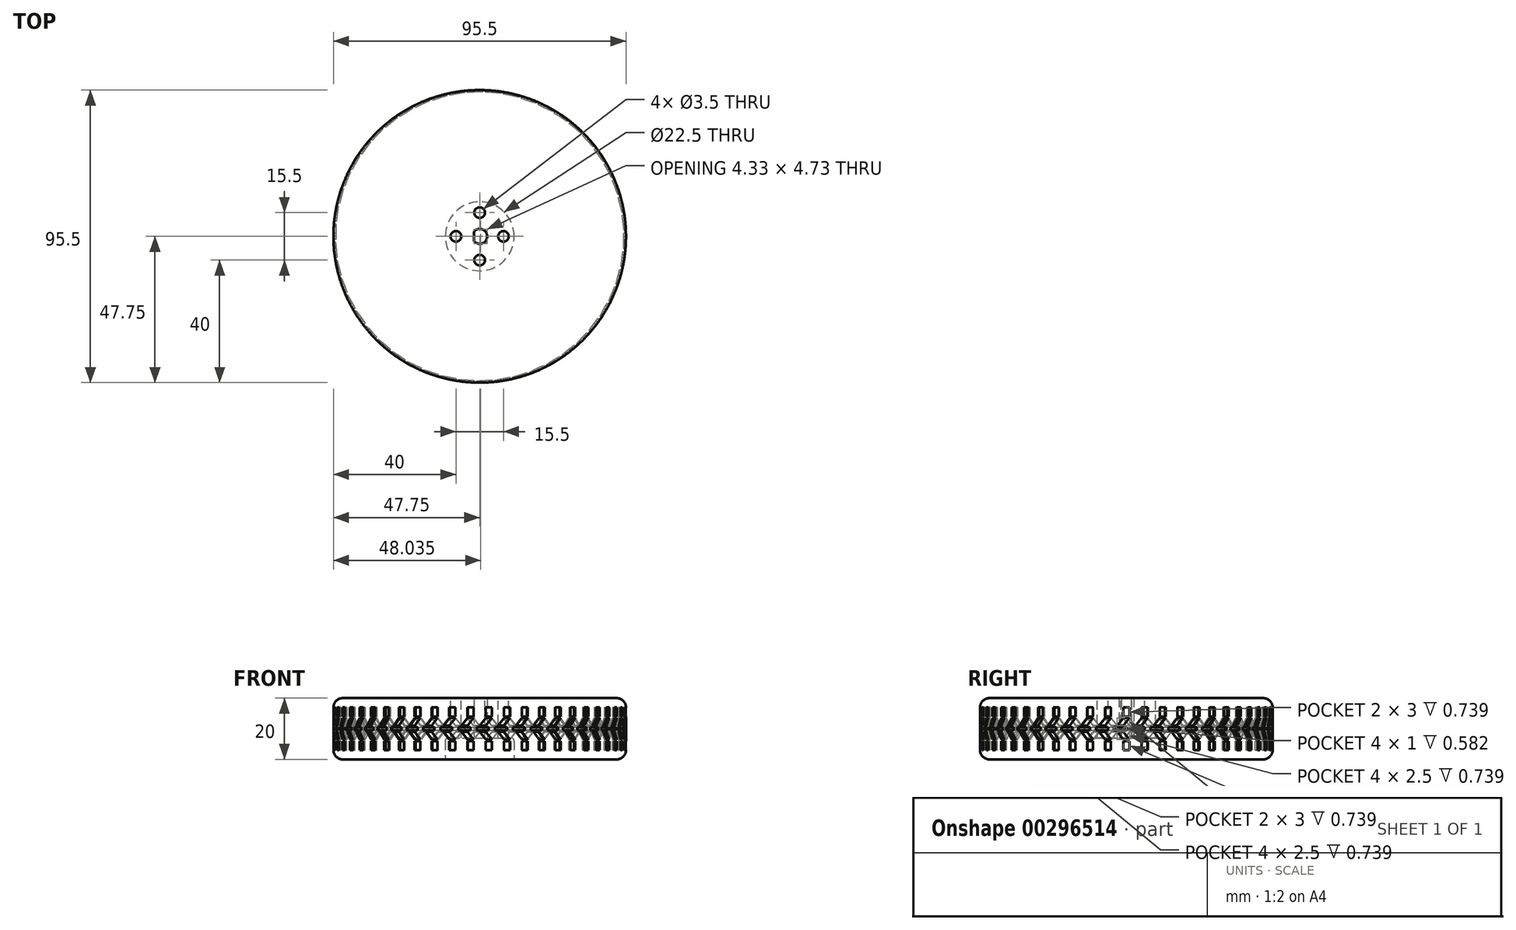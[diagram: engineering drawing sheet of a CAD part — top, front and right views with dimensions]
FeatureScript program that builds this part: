
annotation { "Feature Type Name" : "Feature", "Feature Type Description" : "" }
export const myFeature = defineFeature(function(context is Context, id is Id, definition is map)
    precondition{}
    {
        {
            assignVariable(context, id + "F0", {"name" : "TreadCount", "anyValue" : 50});
        }
        {
            var Q0;
            Q0=qCreatedBy(makeId("Top.planeOp"),FACE);
            var sketch = newSketch(context, id + "F1", { "sketchPlane" : qUnion([Q0])});
            skCircle(sketch, "E0", {"center": v(0, 0) * mm, "radius": 47.75 * mm});
            skCircle(sketch, "E1", {"center": v(0, 0) * mm, "radius": 44 * mm});
            skArc(sketch, "E2", {"start": v(-1.88, -1.57) * mm, "mid": v(2.45, 0) * mm, "end": v(-1.88, 1.57) * mm});
            skLineSegment(sketch, "E3", {"start": v(-1.88, -1.57) * mm, "end": v(-1.88, 1.57) * mm});
            skCircle(sketch, "E4", {"center": v(0, 0) * mm, "radius": 42.5 * mm});
            skCircle(sketch, "E5", {"center": v(0, 0) * mm, "radius": 36 * mm});
            skSolve(sketch);
        }
        {
            var Q0;
            Q0=makeQuery(id+"F1.imprint","IMPRINT",FACE,{"disambiguationData":[TD([[makeQuery(id+"F1.imprint","IMPRINT",EDGE,{"derivedFrom":sQuery(id+"F1.wireOp",EDGE,"E2")}),-1.0]])]});
            var Q1;
            Q1=makeQuery(id+"F1.imprint","IMPRINT",FACE,{"disambiguationData":[TD([[makeQuery(id+"F1.imprint","IMPRINT",EDGE,{"derivedFrom":sQuery(id+"F1.wireOp",EDGE,"8wvdLqEF-Mvgu-ieMB-92kP-JiN9EquYggHF")}),1.0]])]});
            extrude(context, id + "F2", {"entities" : qUnion([Q0, Q1]), "depth" : 12.5 * mm, "hasSecondDirection" : true, "secondDirectionOppositeDirection" : false, "secondDirectionDepth" : 7.5 * mm});
        }
        {
            var Q0;
            Q0=makeQuery(id+"F1.imprint","IMPRINT",FACE,{"disambiguationData":[TD([[makeQuery(id+"F1.imprint","IMPRINT",EDGE,{"derivedFrom":sQuery(id+"F1.wireOp",EDGE,"E4")}),1.0]])]});
            var Q1;
            Q1=makeQuery(id+"F1.imprint","IMPRINT",FACE,{"disambiguationData":[TD([[makeQuery(id+"F1.imprint","IMPRINT",EDGE,{"derivedFrom":sQuery(id+"F1.wireOp",EDGE,"E1")}),1.0]])]});
            var Q2;
            Q2=makeQuery(id+"F1.imprint","IMPRINT",FACE,{"disambiguationData":[TD([[makeQuery(id+"F1.imprint","IMPRINT",EDGE,{"derivedFrom":sQuery(id+"F1.wireOp",EDGE,"E2")}),-1.0]])]});
            extrude(context, id + "F3", {"entities" : qUnion([Q0, Q1, Q2]), "operationType" : NewBodyOperationType.ADD, "depth" : 20 * mm});
        }
        {
            var Q0;
            Q0=makeQuery(id+"F1.imprint","IMPRINT",FACE,{"disambiguationData":[TD([[makeQuery(id+"F1.imprint","IMPRINT",EDGE,{"derivedFrom":sQuery(id+"F1.wireOp",EDGE,"E0")}),1.0]])]});
            extrude(context, id + "F4", {"entities" : qUnion([Q0]), "depth" : 20 * mm});
        }
        {
            var Q0;
            Q0=makeQuery(id+"F1.imprint","IMPRINT",FACE,{"disambiguationData":[TD([[makeQuery(id+"F1.imprint","IMPRINT",EDGE,{"derivedFrom":sQuery(id+"F1.wireOp",EDGE,"E1")}),1.0]])]});
            extrude(context, id + "F5", {"entities" : qUnion([Q0]), "operationType" : NewBodyOperationType.REMOVE, "depth" : 1 * mm});
        }
        {
            var Q0;
            Q0=makeQuery(id+"F1.imprint","IMPRINT",FACE,{"disambiguationData":[TD([[makeQuery(id+"F1.imprint","IMPRINT",EDGE,{"derivedFrom":sQuery(id+"F1.wireOp",EDGE,"E1")}),1.0]])]});
            extrude(context, id + "F6", {"entities" : qUnion([Q0]), "operationType" : NewBodyOperationType.ADD, "depth" : 1 * mm});
        }
        {
            var Q0;
            Q0=makeQuery(id+"F1.imprint","IMPRINT",FACE,{"disambiguationData":[TD([[makeQuery(id+"F1.imprint","IMPRINT",EDGE,{"derivedFrom":sQuery(id+"F1.wireOp",EDGE,"E1")}),1.0]])]});
            extrude(context, id + "F7", {"entities" : qUnion([Q0]), "operationType" : NewBodyOperationType.REMOVE, "depth" : 20 * mm, "hasSecondDirection" : true, "secondDirectionOppositeDirection" : false, "secondDirectionDepth" : 19 * mm});
        }
        {
            var Q0;
            Q0=makeQuery(id+"F1.imprint","IMPRINT",FACE,{"disambiguationData":[TD([[makeQuery(id+"F1.imprint","IMPRINT",EDGE,{"derivedFrom":sQuery(id+"F1.wireOp",EDGE,"E1")}),1.0]])]});
            extrude(context, id + "F8", {"entities" : qUnion([Q0]), "operationType" : NewBodyOperationType.ADD, "depth" : 20 * mm, "hasSecondDirection" : true, "secondDirectionOppositeDirection" : false, "secondDirectionDepth" : 19 * mm});
        }
        {
            var Q0;
            Q0=qCreatedBy(makeId("Right.planeOp"),FACE);
            cPlane(context, id + "F9", {"entities" : qUnion([Q0]), "cplaneType" : CPlaneType.OFFSET, "offset" : 48 * mm, "width" : 150 * mm, "height" : 150 * mm});
        }
        {
            var Q0;
            Q0=qCreatedBy(id+"F9.planeOp",FACE);
            var sketch = newSketch(context, id + "F10", { "sketchPlane" : qUnion([Q0])});
            skPoint(sketch, "E6", {"position": v(0, 10) * mm});
            skLineSegment(sketch, "E7.bottom", {"start": v(-1, 17) * mm, "end": v(1, 17) * mm});
            skLineSegment(sketch, "E7.top", {"start": v(-1, 14) * mm, "end": v(1, 14) * mm});
            skLineSegment(sketch, "E7.left", {"start": v(-1, 17) * mm, "end": v(-1, 14) * mm});
            skLineSegment(sketch, "E7.right", {"start": v(1, 17) * mm, "end": v(1, 14) * mm});
            skLineSegment(sketch, "E8", {"start": v(0, 10) * mm, "end": v(-8.56, 10) * mm});
            skLineSegment(sketch, "E9.MirrorCS", {"start": v(-1, 6) * mm, "end": v(1, 6) * mm});
            skLineSegment(sketch, "E10.MirrorCS", {"start": v(-1, 3) * mm, "end": v(-1, 6) * mm});
            skLineSegment(sketch, "E11.MirrorCS", {"start": v(1, 3) * mm, "end": v(1, 6) * mm});
            skLineSegment(sketch, "E12.MirrorCS", {"start": v(-1, 3) * mm, "end": v(1, 3) * mm});
            skLineSegment(sketch, "E13.bottom", {"start": v(-1, 13.5) * mm, "end": v(1, 13.5) * mm});
            skPoint(sketch, "E14", {"position": v(-3, 11) * mm});
            skLineSegment(sketch, "E15", {"start": v(-3, 11) * mm, "end": v(-1, 13.5) * mm});
            skLineSegment(sketch, "E16.MirrorCS", {"start": v(-3, 9) * mm, "end": v(-1, 6.5) * mm});
            skLineSegment(sketch, "E17.MirrorCS", {"start": v(-1, 6.5) * mm, "end": v(1, 6.5) * mm});
            skPoint(sketch, "E18", {"position": v(-1, 11) * mm});
            skLineSegment(sketch, "E19", {"start": v(-3, 11) * mm, "end": v(-1, 11) * mm});
            skLineSegment(sketch, "E20", {"start": v(-1, 11) * mm, "end": v(1, 13.5) * mm});
            skLineSegment(sketch, "E21.MirrorCS", {"start": v(-3, 9) * mm, "end": v(-1, 9) * mm});
            skLineSegment(sketch, "E22.MirrorCS", {"start": v(-1, 9) * mm, "end": v(1, 6.5) * mm});
            skLineSegment(sketch, "E23.bottom", {"start": v(-4, 10.5) * mm, "end": v(0, 10.5) * mm});
            skLineSegment(sketch, "E23.top", {"start": v(-4, 9.5) * mm, "end": v(0, 9.5) * mm});
            skLineSegment(sketch, "E23.left", {"start": v(-4, 10.5) * mm, "end": v(-4, 9.5) * mm});
            skLineSegment(sketch, "E23.right", {"start": v(0, 10.5) * mm, "end": v(0, 9.5) * mm});
            skPoint(sketch, "E23.middle", {"position": v(-2, 10) * mm});
            skSolve(sketch);
        }
        {
            var Q0;
            Q0=makeQuery(id+"F10.imprint","IMPRINT",FACE,{"disambiguationData":[TD([[makeQuery(id+"F10.imprint","IMPRINT",EDGE,{"derivedFrom":sQuery(id+"F10.wireOp",EDGE,"E7.bottom")}),-1.0]])]});
            var Q1;
            Q1=makeQuery(id+"F10.imprint","IMPRINT",FACE,{"disambiguationData":[TD([[makeQuery(id+"F10.imprint","IMPRINT",EDGE,{"derivedFrom":sQuery(id+"F10.wireOp",EDGE,"E13.bottom")}),-1.0]])]});
            var Q2;
            Q2=makeQuery(id+"F10.imprint","IMPRINT",FACE,{"disambiguationData":[TD([[makeQuery(id+"F10.imprint","IMPRINT",EDGE,{"derivedFrom":sQuery(id+"F10.wireOp",EDGE,"c6fea6ce-3147-4b6b-9fa2-a9a93d3b0bdf0.MirrorCS")}),-1.0]])]});
            var Q3;
            Q3=makeQuery(id+"F10.imprint","IMPRINT",FACE,{"disambiguationData":[TD([[makeQuery(id+"F10.imprint","IMPRINT",EDGE,{"derivedFrom":sQuery(id+"F10.wireOp",EDGE,"E9.MirrorCS")}),-1.0]])]});
            var Q4;
            Q4=makeQuery(id+"F10.imprint","IMPRINT",FACE,{"disambiguationData":[TD([[makeQuery(id+"F10.imprint","IMPRINT",EDGE,{"derivedFrom":sQuery(id+"F10.wireOp",EDGE,"E16.MirrorCS")}),1.0]])]});
            var Q5;
            {var subQ5=sQuery(id+"F10.wireOp",EDGE,"E23.top");Q5=makeQuery(id+"F10.imprint","IMPRINT",FACE,{"disambiguationData":[TD([[makeQuery(id+"F10.imprint","IMPRINT",EDGE,{"derivedFrom":subQ5}),1.0]])]});}
            var Q6;
            {var subQ5=sQuery(id+"F10.wireOp",EDGE,"E23.bottom");Q6=makeQuery(id+"F10.imprint","IMPRINT",FACE,{"disambiguationData":[TD([[makeQuery(id+"F10.imprint","IMPRINT",EDGE,{"derivedFrom":subQ5}),-1.0]])]});}
            extrude(context, id + "F11", {"entities" : qUnion([Q0, Q1, Q2, Q3, Q4, Q5, Q6]), "oppositeDirection" : true, "depth" : 1 * mm, "hasSecondDirection" : true, "secondDirectionOppositeDirection" : false, "secondDirectionDepth" : 5 * mm});
        }
        {
            var Q0;
            Q0=makeQuery(id+"F11.opExtrude","SWEPT_BODY",BODY,{"disambiguationData":[OSD([sQuery(id+"F10.wireOp",EDGE,"E23.bottom"),sQuery(id+"F10.wireOp",EDGE,"E23.top"),sQuery(id+"F10.wireOp",EDGE,"E23.left"),sQuery(id+"F10.wireOp",EDGE,"E23.right")])]});
            var Q1;
            Q1=makeQuery(id+"F11.opExtrude","SWEPT_BODY",BODY,{"disambiguationData":[OSD([sQuery(id+"F10.wireOp",EDGE,"E13.bottom"),sQuery(id+"F10.wireOp",EDGE,"E15"),sQuery(id+"F10.wireOp",EDGE,"E19"),sQuery(id+"F10.wireOp",EDGE,"E20")])]});
            var Q2;
            Q2=makeQuery(id+"F11.opExtrude","SWEPT_BODY",BODY,{"disambiguationData":[OSD([sQuery(id+"F10.wireOp",EDGE,"E7.bottom"),sQuery(id+"F10.wireOp",EDGE,"E7.top"),sQuery(id+"F10.wireOp",EDGE,"E7.left"),sQuery(id+"F10.wireOp",EDGE,"E7.right")])]});
            var Q3;
            Q3=makeQuery(id+"F11.opExtrude","SWEPT_BODY",BODY,{"disambiguationData":[OSD([sQuery(id+"F10.wireOp",EDGE,"E16.MirrorCS"),sQuery(id+"F10.wireOp",EDGE,"E17.MirrorCS"),sQuery(id+"F10.wireOp",EDGE,"E21.MirrorCS"),sQuery(id+"F10.wireOp",EDGE,"E22.MirrorCS")])]});
            var Q4;
            Q4=makeQuery(id+"F11.opExtrude","SWEPT_BODY",BODY,{"disambiguationData":[OSD([sQuery(id+"F10.wireOp",EDGE,"E9.MirrorCS"),sQuery(id+"F10.wireOp",EDGE,"E10.MirrorCS"),sQuery(id+"F10.wireOp",EDGE,"E11.MirrorCS"),sQuery(id+"F10.wireOp",EDGE,"E12.MirrorCS")])]});
            var Q5;
            Q5=makeQuery(id+"F4.opExtrude","CAP_EDGE",EDGE,{"disambiguationData":[OSD([sQuery(id+"F1.wireOp",EDGE,"E0")])],"isStart":false});
            circularPattern(context, id + "F12", {"operationType" : NewBodyOperationType.REMOVE, "entities" : qUnion([Q0, Q1, Q2, Q3, Q4]), "axis" : qUnion([Q5]), "angle" : 360 * degree, "instanceCount" : getVariable(context, 'TreadCount'), "equalSpace" : true});
        }
        {
            var Q0;
            Q0=makeQuery(id+"F4.opExtrude","CAP_EDGE",EDGE,{"disambiguationData":[OSD([sQuery(id+"F1.wireOp",EDGE,"E0")])],"isStart":false});
            var Q1;
            Q1=makeQuery(id+"F4.opExtrude","CAP_EDGE",EDGE,{"disambiguationData":[OSD([sQuery(id+"F1.wireOp",EDGE,"E0")])],"isStart":true});
            fillet(context, id + "F13", {"entities" : qUnion([Q0, Q1]), "radius" : 3 * mm, "tangentPropagation" : true, "allowEdgeOverflow" : false});
        }
        {
            var Q0;
            Q0=makeQuery(id+"F3.opExtrude","CAP_FACE",FACE,{"disambiguationData":[OSD([sQuery(id+"F1.wireOp",EDGE,"E1"),sQuery(id+"F1.wireOp",EDGE,"E2"),sQuery(id+"F1.wireOp",EDGE,"E3")])],"isStart":true});
            var sketch = newSketch(context, id + "F14", { "sketchPlane" : qUnion([Q0])});
            skCircle(sketch, "E24", {"center": v(0, 0) * mm, "radius": 11.25 * mm});
            skCircle(sketch, "E25", {"center": v(0, 0) * mm, "radius": 2.5 * mm});
            skCircle(sketch, "E26", {"center": v(0, 7.75) * mm, "radius": 1.75 * mm});
            skSolve(sketch);
        }
        {
            var Q0;
            Q0=makeQuery(id+"F14.imprint","IMPRINT",FACE,{"disambiguationData":[TD([[makeQuery(id+"F14.imprint","IMPRINT",EDGE,{"derivedFrom":sQuery(id+"F14.wireOp",EDGE,"E24")}),1.0]])]});
            var Q1;
            Q1=makeQuery(id+"F14.imprint","IMPRINT",FACE,{"disambiguationData":[TD([[makeQuery(id+"F14.imprint","IMPRINT",EDGE,{"derivedFrom":sQuery(id+"F14.wireOp",EDGE,"E26")}),1.0]])]});
            var Q2;
            Q2=makeQuery(id+"F14.imprint","IMPRINT",FACE,{"disambiguationData":[TD([[makeQuery(id+"F14.imprint","IMPRINT",EDGE,{"derivedFrom":makeQuery(id+"F3.opExtrude","CAP_EDGE",EDGE,{"disambiguationData":[OSD([sQuery(id+"F1.wireOp",EDGE,"E2")])],"isStart":true})}),-1.0]])]});
            var Q3;
            Q3=makeQuery(id+"F14.imprint","IMPRINT",FACE,{"disambiguationData":[TD([[makeQuery(id+"F14.imprint","IMPRINT",EDGE,{"derivedFrom":sQuery(id+"F14.wireOp",EDGE,"E25")}),1.0]])]});
            extrude(context, id + "F15", {"entities" : qUnion([Q0, Q1, Q2, Q3]), "operationType" : NewBodyOperationType.REMOVE, "oppositeDirection" : true, "depth" : 7 * mm});
        }
        {
            var Q0;
            Q0=makeQuery(id+"F14.imprint","IMPRINT",FACE,{"disambiguationData":[TD([[makeQuery(id+"F14.imprint","IMPRINT",EDGE,{"derivedFrom":sQuery(id+"F14.wireOp",EDGE,"E26")}),1.0]])]});
            extrude(context, id + "F16", {"entities" : qUnion([Q0]), "depth" : 25 * mm, "hasSecondDirection" : true, "secondDirectionOppositeDirection" : true, "secondDirectionDepth" : 25 * mm});
        }
        {
            var Q0;
            Q0=makeQuery(id+"F16.opExtrude","SWEPT_BODY",BODY,{"disambiguationData":[OSD([sQuery(id+"F14.wireOp",EDGE,"E26")])]});
            var Q1;
            Q1=sQuery(id+"F14.wireOp",EDGE,"E24");
            circularPattern(context, id + "F17", {"operationType" : NewBodyOperationType.REMOVE, "entities" : qUnion([Q0]), "axis" : qUnion([Q1]), "angle" : 360 * degree, "instanceCount" : 4, "equalSpace" : true});
        }
        {
            var Q0;
            Q0=makeQuery(id+"F15.boolean.opBoolean","COPY",EDGE,{"derivedFrom":makeQuery(id+"F15.opExtrude","CAP_EDGE",EDGE,{"disambiguationData":[OSD([sQuery(id+"F14.wireOp",EDGE,"E24")])],"isStart":true})});
            var Q1;
            Q1=makeQuery(id+"F15.boolean.opBoolean","COPY",EDGE,{"derivedFrom":makeQuery(id+"F15.opExtrude","CAP_EDGE",EDGE,{"disambiguationData":[OSD([sQuery(id+"F14.wireOp",EDGE,"E24")])],"isStart":false})});
            fillet(context, id + "F18", {"entities" : qUnion([Q0, Q1]), "radius" : 1 * mm, "tangentPropagation" : true, "allowEdgeOverflow" : false});
        }
    });
